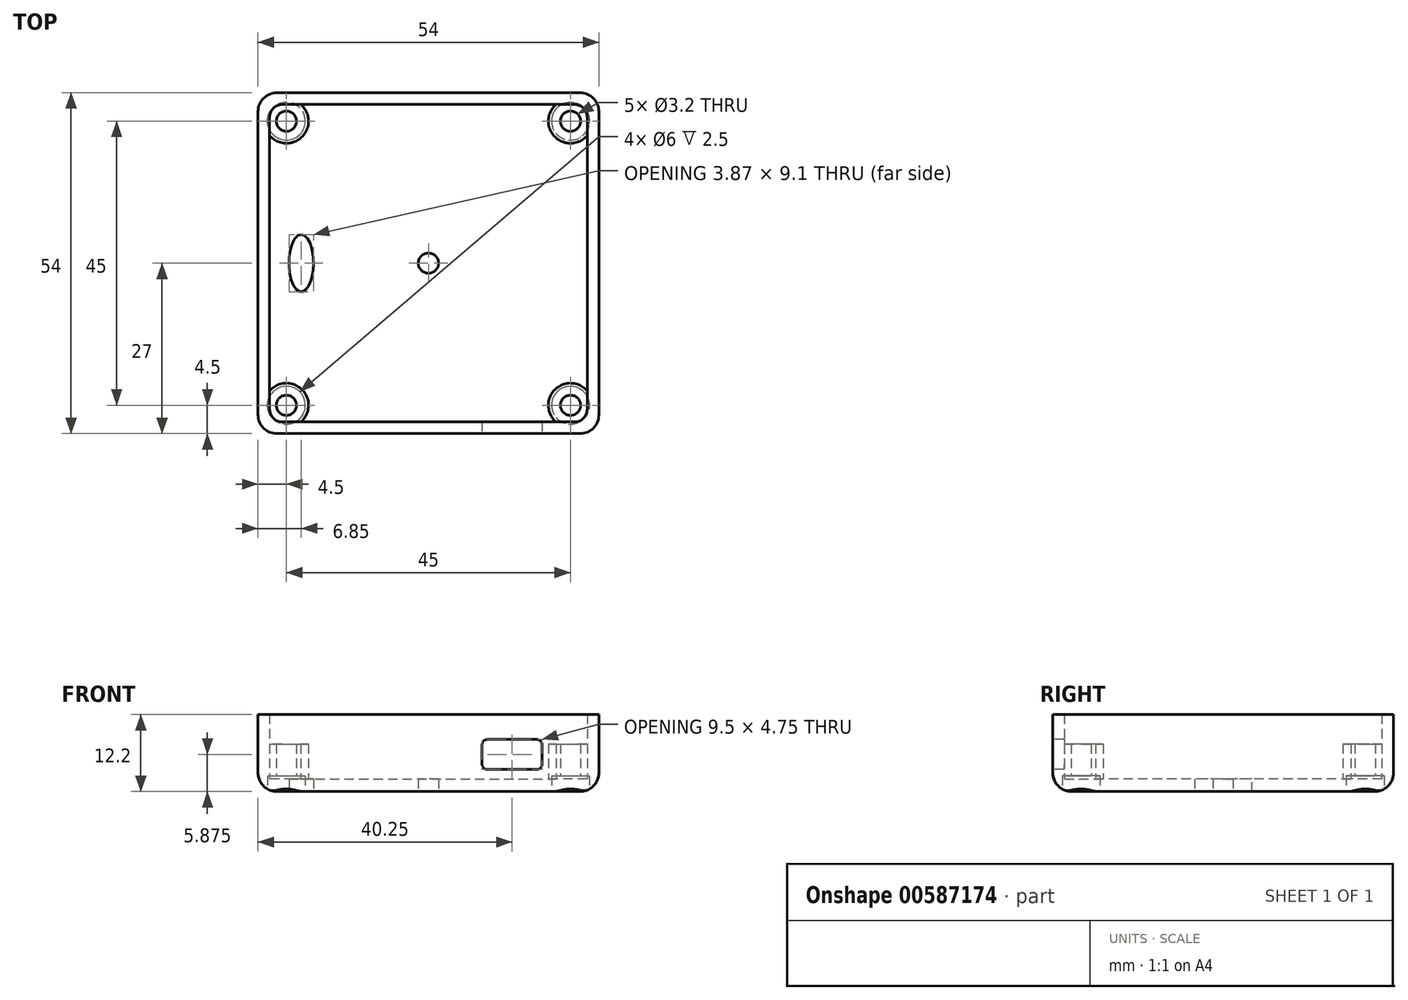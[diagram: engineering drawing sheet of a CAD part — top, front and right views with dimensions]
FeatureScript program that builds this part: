
annotation { "Feature Type Name" : "Feature", "Feature Type Description" : "" }
export const myFeature = defineFeature(function(context is Context, id is Id, definition is map)
    precondition{}
    {
        {
            var Q0;
            Q0=qCreatedBy(makeId("Top.planeOp"),FACE);
            var sketch = newSketch(context, id + "F0", { "sketchPlane" : qUnion([Q0])});
            skLineSegment(sketch, "E0.bottom", {"start": v(-27, 27) * mm, "end": v(27, 27) * mm});
            skLineSegment(sketch, "E0.top", {"start": v(-27, -27) * mm, "end": v(27, -27) * mm});
            skLineSegment(sketch, "E0.left", {"start": v(-27, 27) * mm, "end": v(-27, -27) * mm});
            skLineSegment(sketch, "E0.right", {"start": v(27, 27) * mm, "end": v(27, -27) * mm});
            skSolve(sketch);
        }
        {
            var Q0;
            Q0 = qSketchRegion(id + "F0", true);
            extrude(context, id + "F1", {"entities" : qUnion([Q0]), "depth" : 2 * mm, "offsetDistance" : 25 * mm});
        }
        {
            var Q0;
            Q0=makeQuery(id+"F1.opExtrude","CAP_FACE",FACE,{"disambiguationData":[OSD([sQuery(id+"F0.wireOp",EDGE,"E0.bottom"),sQuery(id+"F0.wireOp",EDGE,"E0.top"),sQuery(id+"F0.wireOp",EDGE,"E0.left"),sQuery(id+"F0.wireOp",EDGE,"E0.right")])],"isStart":false});
            var sketch = newSketch(context, id + "F2", { "sketchPlane" : qUnion([Q0])});
            skLineSegment(sketch, "E1.bottom", {"start": v(-27, 27) * mm, "end": v(27, 27) * mm});
            skLineSegment(sketch, "E1.top", {"start": v(-27, -27) * mm, "end": v(27, -27) * mm});
            skLineSegment(sketch, "E1.left", {"start": v(-27, 27) * mm, "end": v(-27, -27) * mm});
            skLineSegment(sketch, "E1.right", {"start": v(27, 27) * mm, "end": v(27, -27) * mm});
            skLineSegment(sketch, "E2.bottom", {"start": v(-25.15, 25.15) * mm, "end": v(25.15, 25.15) * mm});
            skLineSegment(sketch, "E2.top", {"start": v(-25.15, -25.15) * mm, "end": v(25.15, -25.15) * mm});
            skLineSegment(sketch, "E2.left", {"start": v(-25.15, 25.15) * mm, "end": v(-25.15, -25.15) * mm});
            skLineSegment(sketch, "E2.right", {"start": v(25.15, 25.15) * mm, "end": v(25.15, -25.15) * mm});
            skSolve(sketch);
        }
        {
            var Q0;
            Q0 = qSketchRegion(id + "F2", true);
            extrude(context, id + "F3", {"entities" : qUnion([Q0]), "operationType" : NewBodyOperationType.ADD, "depth" : 10.2 * mm, "offsetDistance" : 25 * mm});
        }
        {
            var Q0;
            Q0=makeQuery(id+"F1.opExtrude","CAP_FACE",FACE,{"disambiguationData":[OSD([sQuery(id+"F0.wireOp",EDGE,"E0.bottom"),sQuery(id+"F0.wireOp",EDGE,"E0.top"),sQuery(id+"F0.wireOp",EDGE,"E0.left"),sQuery(id+"F0.wireOp",EDGE,"E0.right")])],"isStart":false});
            var sketch = newSketch(context, id + "F4", { "sketchPlane" : qUnion([Q0])});
            skLineSegment(sketch, "E3.bottom", {"start": v(-22.5, 22.5) * mm, "end": v(22.5, 22.5) * mm, "construction": true});
            skLineSegment(sketch, "E3.top", {"start": v(-22.5, -22.5) * mm, "end": v(22.5, -22.5) * mm, "construction": true});
            skLineSegment(sketch, "E3.left", {"start": v(-22.5, 22.5) * mm, "end": v(-22.5, -22.5) * mm, "construction": true});
            skLineSegment(sketch, "E3.right", {"start": v(22.5, 22.5) * mm, "end": v(22.5, -22.5) * mm, "construction": true});
            skCircle(sketch, "E4", {"center": v(-22.5, 22.5) * mm, "radius": 3.5 * mm});
            skCircle(sketch, "E5", {"center": v(22.5, 22.5) * mm, "radius": 3.5 * mm});
            skCircle(sketch, "E6", {"center": v(22.5, -22.5) * mm, "radius": 3.5 * mm});
            skCircle(sketch, "E7", {"center": v(-22.5, -22.5) * mm, "radius": 3.5 * mm});
            skSolve(sketch);
        }
        {
            var Q0;
            Q0 = qSketchRegion(id + "F4", true);
            extrude(context, id + "F5", {"entities" : qUnion([Q0]), "operationType" : NewBodyOperationType.ADD, "depth" : 5.5 * mm, "offsetDistance" : 25 * mm});
        }
        {
            var Q0;
            Q0=makeQuery(id+"F1.opExtrude","CAP_FACE",FACE,{"disambiguationData":[OSD([sQuery(id+"F0.wireOp",EDGE,"E0.bottom"),sQuery(id+"F0.wireOp",EDGE,"E0.top"),sQuery(id+"F0.wireOp",EDGE,"E0.left"),sQuery(id+"F0.wireOp",EDGE,"E0.right")])],"isStart":true});
            var sketch = newSketch(context, id + "F6", { "sketchPlane" : qUnion([Q0])});
            skLineSegment(sketch, "E8.bottom", {"start": v(-22.5, 22.5) * mm, "end": v(22.5, 22.5) * mm, "construction": true});
            skLineSegment(sketch, "E8.top", {"start": v(-22.5, -22.5) * mm, "end": v(22.5, -22.5) * mm, "construction": true});
            skLineSegment(sketch, "E8.left", {"start": v(-22.5, 22.5) * mm, "end": v(-22.5, -22.5) * mm, "construction": true});
            skLineSegment(sketch, "E8.right", {"start": v(22.5, 22.5) * mm, "end": v(22.5, -22.5) * mm, "construction": true});
            skCircle(sketch, "E9", {"center": v(-22.5, 22.5) * mm, "radius": 1.6 * mm});
            skCircle(sketch, "E10", {"center": v(22.5, 22.5) * mm, "radius": 1.6 * mm});
            skCircle(sketch, "E11", {"center": v(22.5, -22.5) * mm, "radius": 1.6 * mm});
            skCircle(sketch, "E12", {"center": v(-22.5, -22.5) * mm, "radius": 1.6 * mm});
            skCircle(sketch, "E13", {"center": v(0, 0) * mm, "radius": 1.6 * mm});
            skSolve(sketch);
        }
        {
            var Q0;
            Q0 = qSketchRegion(id + "F6", true);
            extrude(context, id + "F7", {"entities" : qUnion([Q0]), "operationType" : NewBodyOperationType.REMOVE, "oppositeDirection" : true, "depth" : 25 * mm, "offsetDistance" : 25 * mm});
        }
        {
            var Q0;
            Q0=makeQuery(id+"F3.boolean.opBoolean","MERGE",FACE,{"derivedFrom":[makeQuery(id+"F1.opExtrude","SWEPT_FACE",FACE,{"disambiguationData":[OSD([sQuery(id+"F0.wireOp",EDGE,"E0.top")])]}),makeQuery(id+"F3.opExtrude","SWEPT_FACE",FACE,{"disambiguationData":[OSD([sQuery(id+"F2.wireOp",EDGE,"E1.top")])]})]});
            var sketch = newSketch(context, id + "F8", { "sketchPlane" : qUnion([Q0])});
            skLineSegment(sketch, "E14.bottom", {"start": v(8.5, 3.5) * mm, "end": v(18, 3.5) * mm});
            skLineSegment(sketch, "E14.top", {"start": v(8.5, 8.25) * mm, "end": v(18, 8.25) * mm});
            skLineSegment(sketch, "E14.left", {"start": v(8.5, 3.5) * mm, "end": v(8.5, 8.25) * mm});
            skLineSegment(sketch, "E14.right", {"start": v(18, 3.5) * mm, "end": v(18, 8.25) * mm});
            skSolve(sketch);
        }
        {
            var Q0;
            Q0 = qSketchRegion(id + "F8", true);
            extrude(context, id + "F9", {"entities" : qUnion([Q0]), "operationType" : NewBodyOperationType.REMOVE, "oppositeDirection" : true, "depth" : 25 * mm, "offsetDistance" : 25 * mm});
        }
        {
            var Q0;
            Q0=makeQuery(id+"F5.boolean.opBoolean","SPLIT",FACE,{"disambiguationData":[TD([makeQuery(id+"F3.opExtrude","SWEPT_FACE",FACE,{"disambiguationData":[OSD([sQuery(id+"F2.wireOp",EDGE,"E2.bottom")])]}),makeQuery(id+"F3.opExtrude","SWEPT_FACE",FACE,{"disambiguationData":[OSD([sQuery(id+"F2.wireOp",EDGE,"E2.top")])]}),makeQuery(id+"F3.opExtrude","SWEPT_FACE",FACE,{"disambiguationData":[OSD([sQuery(id+"F2.wireOp",EDGE,"E2.left")])]}),makeQuery(id+"F3.opExtrude","SWEPT_FACE",FACE,{"disambiguationData":[OSD([sQuery(id+"F2.wireOp",EDGE,"E2.right")])]}),makeQuery(id+"F5.opExtrude","SWEPT_FACE",FACE,{"disambiguationData":[OSD([sQuery(id+"F4.wireOp",EDGE,"E4")])]}),makeQuery(id+"F5.opExtrude","SWEPT_FACE",FACE,{"disambiguationData":[OSD([sQuery(id+"F4.wireOp",EDGE,"E5")])]}),makeQuery(id+"F5.opExtrude","SWEPT_FACE",FACE,{"disambiguationData":[OSD([sQuery(id+"F4.wireOp",EDGE,"E6")])]}),makeQuery(id+"F5.opExtrude","SWEPT_FACE",FACE,{"disambiguationData":[OSD([sQuery(id+"F4.wireOp",EDGE,"E7")])]})])],"derivedFrom":makeQuery(id+"F1.opExtrude","CAP_FACE",FACE,{"disambiguationData":[OSD([sQuery(id+"F0.wireOp",EDGE,"E0.bottom"),sQuery(id+"F0.wireOp",EDGE,"E0.top"),sQuery(id+"F0.wireOp",EDGE,"E0.left"),sQuery(id+"F0.wireOp",EDGE,"E0.right")])],"isStart":false})});
            var sketch = newSketch(context, id + "F10", { "sketchPlane" : qUnion([Q0])});
            skEllipse(sketch, "E15", {"center": v(-20.15, 0) * mm, "majorRadius": 4.55 * mm, "minorRadius": 1.94 * mm, "majorAxis": v(0, 1)});
            skSolve(sketch);
        }
        {
            var Q0;
            Q0 = qSketchRegion(id + "F10", true);
            extrude(context, id + "F11", {"entities" : qUnion([Q0]), "operationType" : NewBodyOperationType.REMOVE, "oppositeDirection" : true, "depth" : 25 * mm, "offsetDistance" : 25 * mm});
        }
        {
            var Q0;
            Q0=makeQuery(id+"F1.opExtrude","CAP_EDGE",EDGE,{"disambiguationData":[OSD([sQuery(id+"F0.wireOp",EDGE,"E0.top")])],"isStart":true});
            var Q1;
            Q1=makeQuery(id+"F1.opExtrude","CAP_EDGE",EDGE,{"disambiguationData":[OSD([sQuery(id+"F0.wireOp",EDGE,"E0.left")])],"isStart":true});
            var Q2;
            Q2=makeQuery(id+"F1.opExtrude","CAP_EDGE",EDGE,{"disambiguationData":[OSD([sQuery(id+"F0.wireOp",EDGE,"E0.bottom")])],"isStart":true});
            var Q3;
            Q3=makeQuery(id+"F1.opExtrude","CAP_EDGE",EDGE,{"disambiguationData":[OSD([sQuery(id+"F0.wireOp",EDGE,"E0.right")])],"isStart":true});
            var Q4;
            Q4=makeQuery(id+"F3.boolean.opBoolean","MERGE",EDGE,{"derivedFrom":[makeQuery(id+"F1.opExtrude","SWEPT_EDGE",EDGE,{"disambiguationData":[OSD([sQuery(id+"F0.wireOp",EDGE,"E0.top"),sQuery(id+"F0.wireOp",EDGE,"E0.right")])]}),makeQuery(id+"F3.opExtrude","SWEPT_EDGE",EDGE,{"disambiguationData":[OSD([sQuery(id+"F2.wireOp",EDGE,"E1.top"),sQuery(id+"F2.wireOp",EDGE,"E1.right")])]})]});
            var Q5;
            Q5=makeQuery(id+"F3.boolean.opBoolean","MERGE",EDGE,{"derivedFrom":[makeQuery(id+"F1.opExtrude","SWEPT_EDGE",EDGE,{"disambiguationData":[OSD([sQuery(id+"F0.wireOp",EDGE,"E0.top"),sQuery(id+"F0.wireOp",EDGE,"E0.left")])]}),makeQuery(id+"F3.opExtrude","SWEPT_EDGE",EDGE,{"disambiguationData":[OSD([sQuery(id+"F2.wireOp",EDGE,"E1.top"),sQuery(id+"F2.wireOp",EDGE,"E1.left")])]})]});
            var Q6;
            Q6=makeQuery(id+"F3.boolean.opBoolean","MERGE",EDGE,{"derivedFrom":[makeQuery(id+"F1.opExtrude","SWEPT_EDGE",EDGE,{"disambiguationData":[OSD([sQuery(id+"F0.wireOp",EDGE,"E0.bottom"),sQuery(id+"F0.wireOp",EDGE,"E0.left")])]}),makeQuery(id+"F3.opExtrude","SWEPT_EDGE",EDGE,{"disambiguationData":[OSD([sQuery(id+"F2.wireOp",EDGE,"E1.bottom"),sQuery(id+"F2.wireOp",EDGE,"E1.left")])]})]});
            var Q7;
            Q7=makeQuery(id+"F3.boolean.opBoolean","MERGE",EDGE,{"derivedFrom":[makeQuery(id+"F1.opExtrude","SWEPT_EDGE",EDGE,{"disambiguationData":[OSD([sQuery(id+"F0.wireOp",EDGE,"E0.bottom"),sQuery(id+"F0.wireOp",EDGE,"E0.right")])]}),makeQuery(id+"F3.opExtrude","SWEPT_EDGE",EDGE,{"disambiguationData":[OSD([sQuery(id+"F2.wireOp",EDGE,"E1.bottom"),sQuery(id+"F2.wireOp",EDGE,"E1.right")])]})]});
            fillet(context, id + "F12", {"entities" : qUnion([Q0, Q1, Q2, Q3, Q4, Q5, Q6, Q7]), "radius" : 3 * mm, "tangentPropagation" : true, "allowEdgeOverflow" : false});
        }
        {
            var Q0;
            Q0=makeQuery(id+"F12.opFillet","SPLIT",FACE,{"disambiguationData":[OD(4.0)],"derivedFrom":makeQuery(id+"F1.opExtrude","CAP_FACE",FACE,{"disambiguationData":[OSD([sQuery(id+"F0.wireOp",EDGE,"E0.bottom"),sQuery(id+"F0.wireOp",EDGE,"E0.top"),sQuery(id+"F0.wireOp",EDGE,"E0.left"),sQuery(id+"F0.wireOp",EDGE,"E0.right")])],"isStart":true})});
            var sketch = newSketch(context, id + "F13", { "sketchPlane" : qUnion([Q0])});
            skCircle(sketch, "E16", {"center": v(-22.5, 22.5) * mm, "radius": 3 * mm});
            skCircle(sketch, "E17", {"center": v(22.5, 22.5) * mm, "radius": 3 * mm});
            skCircle(sketch, "E18", {"center": v(22.5, -22.5) * mm, "radius": 3 * mm});
            skCircle(sketch, "E19", {"center": v(-22.5, -22.5) * mm, "radius": 3 * mm});
            skSolve(sketch);
        }
        {
            var Q0;
            Q0 = qSketchRegion(id + "F13", true);
            extrude(context, id + "F14", {"entities" : qUnion([Q0]), "operationType" : NewBodyOperationType.REMOVE, "oppositeDirection" : true, "depth" : 2.5 * mm, "offsetDistance" : 25 * mm});
        }
        {
            var Q0;
            Q0=makeQuery(id+"F9.boolean.opBoolean","COPY",EDGE,{"derivedFrom":makeQuery(id+"F9.opExtrude","SWEPT_EDGE",EDGE,{"disambiguationData":[OSD([sQuery(id+"F8.wireOp",EDGE,"E14.top"),sQuery(id+"F8.wireOp",EDGE,"E14.left")])]})});
            var Q1;
            Q1=makeQuery(id+"F9.boolean.opBoolean","COPY",EDGE,{"derivedFrom":makeQuery(id+"F9.opExtrude","SWEPT_EDGE",EDGE,{"disambiguationData":[OSD([sQuery(id+"F8.wireOp",EDGE,"E14.bottom"),sQuery(id+"F8.wireOp",EDGE,"E14.left")])]})});
            var Q2;
            Q2=makeQuery(id+"F9.boolean.opBoolean","COPY",EDGE,{"derivedFrom":makeQuery(id+"F9.opExtrude","SWEPT_EDGE",EDGE,{"disambiguationData":[OSD([sQuery(id+"F8.wireOp",EDGE,"E14.bottom"),sQuery(id+"F8.wireOp",EDGE,"E14.right")])]})});
            var Q3;
            Q3=makeQuery(id+"F9.boolean.opBoolean","COPY",EDGE,{"derivedFrom":makeQuery(id+"F9.opExtrude","SWEPT_EDGE",EDGE,{"disambiguationData":[OSD([sQuery(id+"F8.wireOp",EDGE,"E14.top"),sQuery(id+"F8.wireOp",EDGE,"E14.right")])]})});
            fillet(context, id + "F15", {"entities" : qUnion([Q0, Q1, Q2, Q3]), "radius" : 0.8 * mm, "tangentPropagation" : true, "allowEdgeOverflow" : false});
        }
        {
            var Q0;
            Q0=makeQuery(id+"F3.opExtrude","SWEPT_EDGE",EDGE,{"disambiguationData":[OSD([sQuery(id+"F2.wireOp",EDGE,"E2.bottom"),sQuery(id+"F2.wireOp",EDGE,"E2.left")])]});
            var Q1;
            Q1=makeQuery(id+"F3.opExtrude","SWEPT_EDGE",EDGE,{"disambiguationData":[OSD([sQuery(id+"F2.wireOp",EDGE,"E2.bottom"),sQuery(id+"F2.wireOp",EDGE,"E2.right")])]});
            var Q2;
            Q2=makeQuery(id+"F3.opExtrude","SWEPT_EDGE",EDGE,{"disambiguationData":[OSD([sQuery(id+"F2.wireOp",EDGE,"E2.top"),sQuery(id+"F2.wireOp",EDGE,"E2.left")])]});
            var Q3;
            Q3=makeQuery(id+"F3.opExtrude","SWEPT_EDGE",EDGE,{"disambiguationData":[OSD([sQuery(id+"F2.wireOp",EDGE,"E2.top"),sQuery(id+"F2.wireOp",EDGE,"E2.right")])]});
            fillet(context, id + "F16", {"entities" : qUnion([Q0, Q1, Q2, Q3]), "radius" : 2 * mm, "tangentPropagation" : true, "allowEdgeOverflow" : false});
        }
    });
